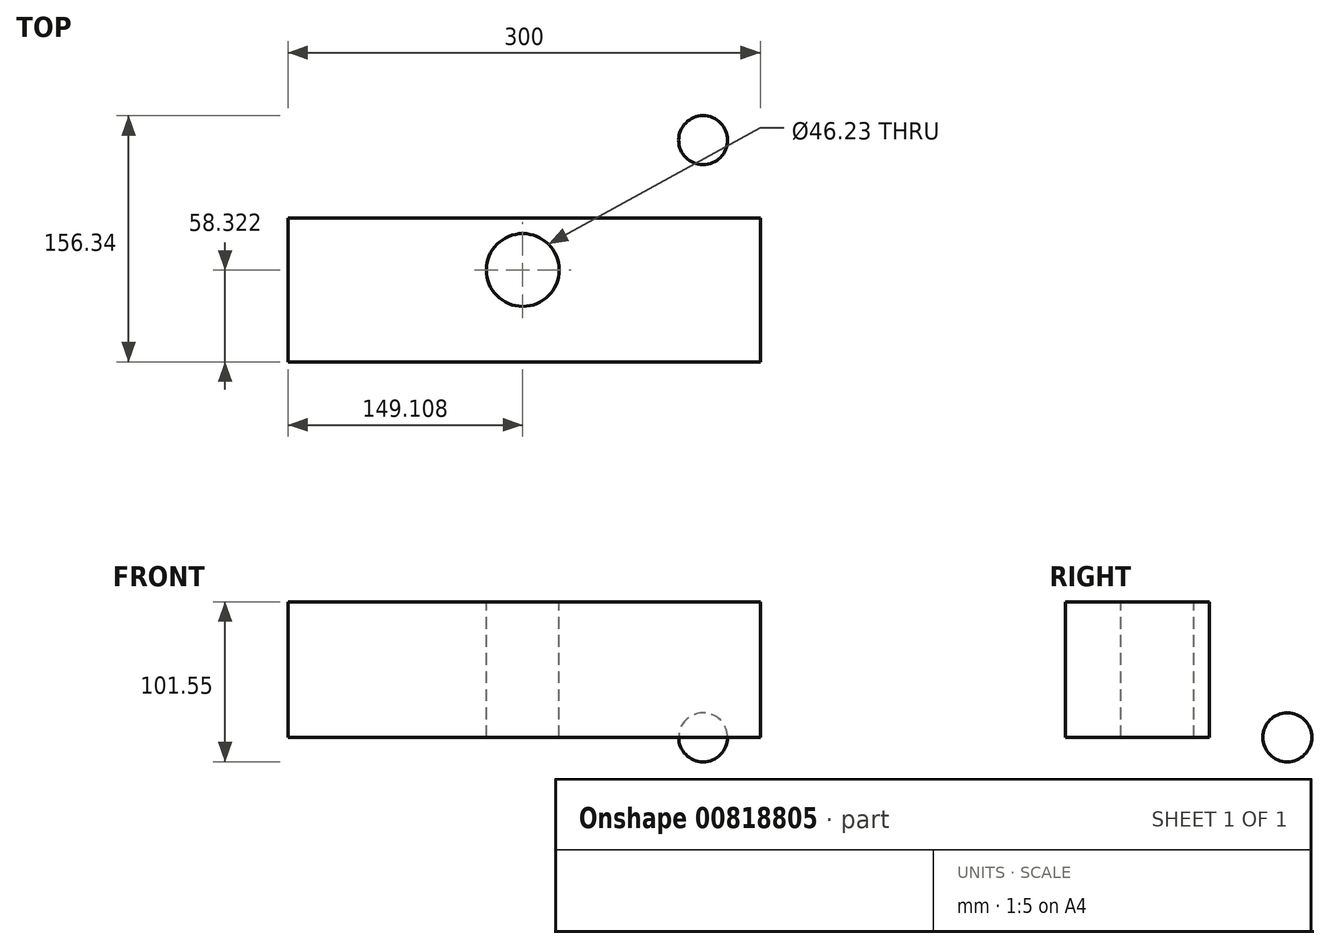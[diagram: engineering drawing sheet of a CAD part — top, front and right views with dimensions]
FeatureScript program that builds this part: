
annotation { "Feature Type Name" : "Feature", "Feature Type Description" : "" }
export const myFeature = defineFeature(function(context is Context, id is Id, definition is map)
    precondition{}
    {
        {
            var Q0;
            Q0=qCreatedBy(makeId("Top.planeOp"),FACE);
            var sketch = newSketch(context, id + "F0", { "sketchPlane" : qUnion([Q0])});
            skLineSegment(sketch, "E0.bottom", {"start": v(0, 0) * mm, "end": v(-300, 0) * mm});
            skLineSegment(sketch, "E0.top", {"start": v(0, -91.42) * mm, "end": v(-300, -91.42) * mm});
            skLineSegment(sketch, "E0.left", {"start": v(0, 0) * mm, "end": v(0, -91.42) * mm});
            skLineSegment(sketch, "E0.right", {"start": v(-300, 0) * mm, "end": v(-300, -91.42) * mm});
            skSolve(sketch);
        }
        {
            var Q0;
            Q0=makeQuery(id+"F0.imprint","IMPRINT",FACE,{"disambiguationData":[TD([[makeQuery(id+"F0.imprint","IMPRINT",EDGE,{"derivedFrom":sQuery(id+"F0.wireOp",EDGE,"E0.bottom")}),1.0]])]});
            extrude(context, id + "F1", {"entities" : qUnion([Q0]), "depth" : 86 * mm, "offsetDistance" : 25 * mm});
        }
        {
            var Q0;
            Q0=makeQuery(id+"F1.opExtrude","CAP_FACE",FACE,{"disambiguationData":[OSD([sQuery(id+"F0.wireOp",EDGE,"E0.bottom"),sQuery(id+"F0.wireOp",EDGE,"E0.top"),sQuery(id+"F0.wireOp",EDGE,"E0.left"),sQuery(id+"F0.wireOp",EDGE,"E0.right")])],"isStart":false});
            var sketch = newSketch(context, id + "F2", { "sketchPlane" : qUnion([Q0])});
            skCircle(sketch, "E1", {"center": v(-150.9, -33.1) * mm, "radius": 23.12 * mm});
            skSolve(sketch);
        }
        {
            var Q0;
            Q0 = qSketchRegion(id + "F2", true);
            extrude(context, id + "F3", {"entities" : qUnion([Q0]), "operationType" : NewBodyOperationType.REMOVE, "oppositeDirection" : true, "depth" : 146 * mm, "offsetDistance" : 25 * mm});
        }
        {
            var Q0;
            Q0=qCreatedBy(makeId("Top.planeOp"),FACE);
            var sketch = newSketch(context, id + "F4", { "sketchPlane" : qUnion([Q0])});
            skArc(sketch, "E2", {"start": v(-20.8, 49.37) * mm, "mid": v(-36.35, 64.92) * mm, "end": v(-51.9, 49.37) * mm});
            skLineSegment(sketch, "E3", {"start": v(-51.9, 49.37) * mm, "end": v(-20.8, 49.37) * mm});
            skSolve(sketch);
        }
        {
            var Q0;
            Q0 = qSketchRegion(id + "F4", true);
            var Q1;
            Q1=sQuery(id+"F4.wireOp",EDGE,"E3");
            revolve(context, id + "F5", {"surfaceOperationType" : NewSurfaceOperationType.NEW, "entities" : qUnion([Q0]), "axis" : qUnion([Q1]), "revolveType" : RevolveType.FULL});
        }
    });
